# Revit family: Drain_Floor_Side_Outlet_Zurn-460B_Shallow_Body
name_source: partatom
category: Plumbing Fixtures
units: mm (PartAtom-declared; Revit-internal decimal feet)

## family parameters
Always vertical = Yes
Cut with Voids When Loaded = No
Maintain Annotation Orientation = No
OmniClass Number = 23.70.50.21.24.14
OmniClass Title = Deck Waste Water Drains
Part Type = Normal
Room Calculation Point = No
Round Connector Dimension = Use Radius
Shared = No
Work Plane-Based = No

## types (24) — shared parameters
Assembly Code = D2030300
CW Connection = No
Default Elevation = 48 "
Description = SHALLOW BODY FLOOR DRAIN W/ SIDE OUTLET AND TYPE B STRAINER
Grate Open Area = 34 "
HW Connection = No
Main Material = Iron - Zurn -Cast - Painted - Blue
Manufacturer = Zurn Water, LLC
Manufacurer Brand = Zurn
Modified Date = 10/23/2025
Product Documentation Link = https://files.zurn.com
Product Page URL = https://www.zurn.com
Product data url = https://www.bimobject.com
Thickness = 0.25 "
URL = www.zurn.com
Vent Connection = No
WFU = 1
Waste Connection = Yes
zero-valued in all types: CWFU, HWFU

## per-type parameters (varying)
| type | Approx. Weight (Lbs) | Dim D | Dim M | E Body Dimension | Grate & Top Material | Grate Dia | Model | Pipe Size 'A' (Inner Radius) | Pipe Size 'A' (Outer Radius) | Pipe Size A Nominal Radius | Strainer Dia B | Strainer Open Area Sq. In. | Type Comments |
| ZB460B-1.5IP-5" TOP | 8 " | 3.25 " | 2 " | 3.156 " | Bronze - Zurn - Polished | 4.874 " | ZB460B | 0.805 " | 0.95 " | 0.75 " | 5 " | 8 SF | ZB460B-1.5 Inch Threaded Outlet with 5" Round top |
| ZB460B-2IP-5" TOP | 8 " | 3.25 " | 1.781 " | 3.219 " | Bronze - Zurn - Polished | 4.874 " | ZB460B | 1.034 " | 1.188 " | 1 " | 5 " | 8 SF | ZB460B-2 Inch Threaded Outlet with 5" Round top |
| ZB460B-1.5NH-5" TOP | 8 " | 4.25 " | 2 " | 2.969 " | Bronze - Zurn - Polished | 4.874 " | ZB460B | 0.805 " | 0.95 " | 0.75 " | 5 " | 8 SF | ZB460B-1.5 Inch No-Hub Outlet with 5" Round top |
| ZB460B-2NH-5" TOP | 8 " | 5 " | 1.781 " | 2.969 " | Bronze - Zurn - Polished | 4.874 " | ZB460B | 1.034 " | 1.188 " | 1 " | 5 " | 8 SF | ZB460B-2 Inch No-Hub  Outlet with 5" Round top |
| ZB460B-1.5IP-6" TOP | 9 " | 3.25 " | 2 " | 3.156 " | Bronze - Zurn - Polished | 5.874 " | ZB460B | 0.805 " | 0.95 " | 0.75 " | 6 " | 9 SF | ZB460B-1.5 Inch Threaded Outlet with 6" Round top |
| ZB460B-2IP-6" TOP | 9 " | 3.25 " | 1.781 " | 3.219 " | Bronze - Zurn - Polished | 5.874 " | ZB460B | 1.034 " | 1.188 " | 1 " | 6 " | 9 SF | ZB460B-2 Inch Threaded Outlet with 6" Round top |
| ZB460B-1.5NH-6" TOP | 9 " | 4.25 " | 2 " | 2.969 " | Bronze - Zurn - Polished | 5.874 " | ZB460B | 0.805 " | 0.95 " | 0.75 " | 6 " | 9 SF | ZB460B-1.5 Inch No-Hub Outlet with 6" Round top |
| ZB460B-2NH-6" TOP | 9 " | 5 " | 1.781 " | 2.969 " | Bronze - Zurn - Polished | 5.874 " | ZB460B | 1.034 " | 1.188 " | 1 " | 6 " | 9 SF | ZB460B-2 Inch No-Hub  Outlet with 6" Round top |
| ZB460B-1.5IP-7" TOP | 10 " | 3.25 " | 2 " | 3.156 " | Bronze - Zurn - Polished | 6.874 " | ZB460B | 0.805 " | 0.95 " | 0.75 " | 7 " | 12 SF | ZB460B-1.5 Inch Threaded Outlet with 7" Round top |
| ZB460B-2IP-7" TOP | 10 " | 3.25 " | 1.781 " | 3.219 " | Bronze - Zurn - Polished | 6.874 " | ZB460B | 1.034 " | 1.188 " | 1 " | 7 " | 12 SF | ZB460B-2 Inch Threaded Outlet with 7" Round top |
| ZB460B-1.5NH-7" TOP | 10 " | 4.25 " | 2 " | 2.969 " | Bronze - Zurn - Polished | 6.874 " | ZB460B | 0.805 " | 0.95 " | 0.75 " | 7 " | 12 SF | ZB460B-1.5 Inch No-Hub Outlet with 7" Round top |
| ZB460B-2NH-7" TOP | 10 " | 5 " | 1.781 " | 2.969 " | Bronze - Zurn - Polished | 6.874 " | ZB460B | 1.034 " | 1.188 " | 1 " | 7 " | 12 SF | ZB460B-2 Inch No-Hub  Outlet with 7" Round top |
| ZN460B-1.5IP-5" TOP | 8 " | 3.25 " | 2 " | 3.156 " | Bronze - Zurn - Polished Nickel | 4.874 " | ZN460B | 0.805 " | 0.95 " | 0.75 " | 5 " | 8 SF | ZN460B-1.5 Inch Threaded Outlet with 5" Round top |
| ZN460B-2IP-5" TOP | 8 " | 3.25 " | 1.781 " | 3.219 " | Bronze - Zurn - Polished Nickel | 4.874 " | ZN460B | 1.034 " | 1.188 " | 1 " | 5 " | 8 SF | ZN460B-2 Inch Threaded Outlet with 5" Round top |
| ZN460B-1.5NH-5" TOP | 8 " | 4.25 " | 2 " | 2.969 " | Bronze - Zurn - Polished Nickel | 4.874 " | ZN460B | 0.805 " | 0.95 " | 0.75 " | 5 " | 8 SF | ZN460B-1.5 Inch No-Hub Outlet with 5" Round top |
| ZN460B-2NH-5" TOP | 8 " | 5 " | 1.781 " | 2.969 " | Bronze - Zurn - Polished Nickel | 4.874 " | ZN460B | 1.034 " | 1.188 " | 1 " | 5 " | 8 SF | ZN460B-2 Inch No-Hub  Outlet with 5" Round top |
| ZN460B-1.5IP-6" TOP | 9 " | 3.25 " | 2 " | 3.156 " | Bronze - Zurn - Polished Nickel | 5.874 " | ZN460B | 0.805 " | 0.95 " | 0.75 " | 6 " | 9 SF | ZN460B-1.5 Inch Threaded Outlet with 6" Round top |
| ZN460B-2IP-6" TOP | 9 " | 3.25 " | 1.781 " | 3.219 " | Bronze - Zurn - Polished Nickel | 5.874 " | ZN460B | 1.034 " | 1.188 " | 1 " | 6 " | 9 SF | ZN460B-2 Inch Threaded Outlet with 6" Round top |
| ZN460B-1.5NH-6" TOP | 9 " | 4.25 " | 2 " | 2.969 " | Bronze - Zurn - Polished Nickel | 5.874 " | ZN460B | 0.805 " | 0.95 " | 0.75 " | 6 " | 9 SF | ZN460B-1.5 Inch No-Hub Outlet with 6" Round top |
| ZN460B-2NH-6" TOP | 9 " | 5 " | 1.781 " | 2.969 " | Bronze - Zurn - Polished Nickel | 5.874 " | ZN460B | 1.034 " | 1.188 " | 1 " | 6 " | 9 SF | ZN460B-2 Inch No-Hub  Outlet with 6" Round top |
| ZN460B-1.5IP-7" TOP | 10 " | 3.25 " | 2 " | 3.156 " | Bronze - Zurn - Polished Nickel | 6.874 " | ZN460B | 0.805 " | 0.95 " | 0.75 " | 7 " | 12 SF | ZN460B-1.5 Inch Threaded Outlet with 7" Round top |
| ZN460B-2IP-7" TOP | 10 " | 3.25 " | 1.781 " | 3.219 " | Bronze - Zurn - Polished Nickel | 6.874 " | ZN460B | 1.034 " | 1.188 " | 1 " | 7 " | 12 SF | ZN460B-2 Inch Threaded Outlet with 7" Round top |
| ZN460B-1.5NH-7" TOP | 10 " | 4.25 " | 2 " | 2.969 " | Bronze - Zurn - Polished Nickel | 6.874 " | ZN460B | 0.805 " | 0.95 " | 0.75 " | 7 " | 12 SF | ZN460B-1.5 Inch No-Hub Outlet with 7" Round top |
| ZN460B-2NH-7" TOP | 10 " | 5 " | 1.781 " | 2.969 " | Bronze - Zurn - Polished Nickel | 6.874 " | ZN460B | 1.034 " | 1.188 " | 1 " | 7 " | 12 SF | ZN460B-2 Inch No-Hub  Outlet with 7" Round top |

## geometry (parser evidence)
native form markers: Sweep x5
no freeform markers — native parametric forms only
